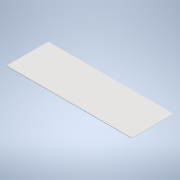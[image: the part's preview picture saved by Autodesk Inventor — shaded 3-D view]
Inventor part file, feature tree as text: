
AUTODESK INVENTOR PART (.ipt)
format: ipt  version: 2022 (Build 260153000, 153)  size: 92,672 bytes
history: native  units: mm
features: other x1, extrude x1, sketch x1
ambient origin geometry x8: Origin, YZ Plane, XZ Plane, XY Plane, X Axis, Y Axis, Z Axis, Center Point
bodies: Body1 (feature_tree)
feature tree (3):
  other  "Твердое тело1"
  extrude  "Выдавливание1"  Depth=500.0mm
  sketch  "Эскиз1"
